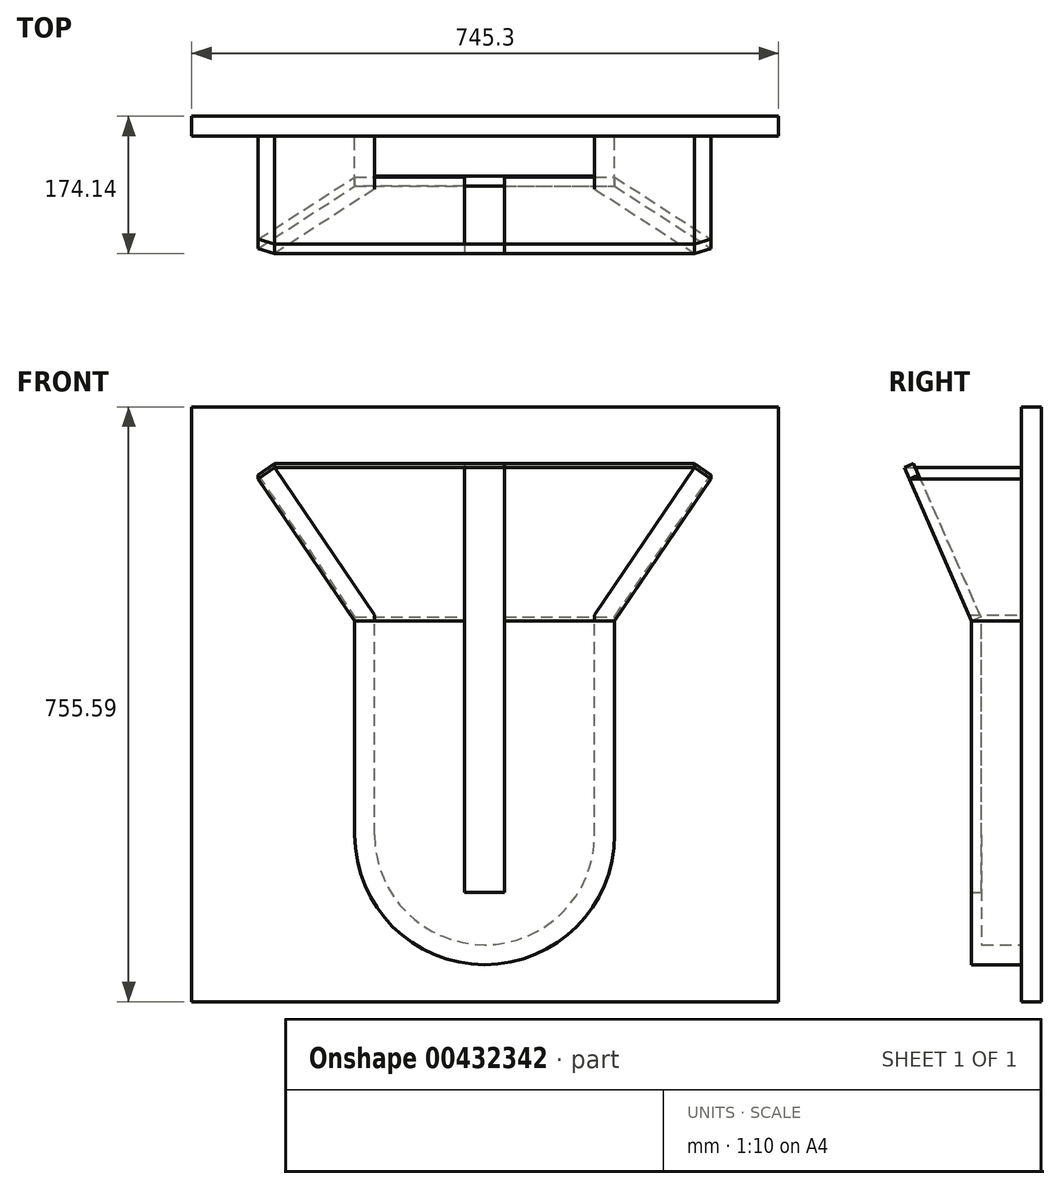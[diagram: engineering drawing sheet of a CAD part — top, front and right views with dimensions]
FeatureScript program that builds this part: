
annotation { "Feature Type Name" : "Feature", "Feature Type Description" : "" }
export const myFeature = defineFeature(function(context is Context, id is Id, definition is map)
    precondition{}
    {
        {
            var Q0;
            Q0=qCreatedBy(makeId("Front.planeOp"),FACE);
            var sketch = newSketch(context, id + "F0", { "sketchPlane" : qUnion([Q0])});
            skLineSegment(sketch, "E0.bottom", {"start": v(-216.96, 293.83) * mm, "end": v(316.44, 293.83) * mm});
            skLineSegment(sketch, "E0.top", {"start": v(-216.96, -337.7) * mm, "end": v(316.44, -337.7) * mm});
            skLineSegment(sketch, "E0.left", {"start": v(-216.96, 248.62) * mm, "end": v(-216.96, -337.7) * mm});
            skLineSegment(sketch, "E0.right", {"start": v(316.44, 248.62) * mm, "end": v(316.44, -337.7) * mm});
            skArc(sketch, "E1", {"start": v(-89.96, -172.6) * mm, "mid": v(49.74, -312.3) * mm, "end": v(189.44, -172.6) * mm});
            skLineSegment(sketch, "E2", {"start": v(-89.96, -172.6) * mm, "end": v(-89.96, 106.8) * mm});
            skLineSegment(sketch, "E3", {"start": v(189.44, -172.6) * mm, "end": v(189.44, 106.8) * mm});
            skLineSegment(sketch, "E4", {"start": v(189.44, 106.8) * mm, "end": v(316.44, 293.83) * mm});
            skLineSegment(sketch, "E5", {"start": v(-89.96, 106.8) * mm, "end": v(-216.96, 293.83) * mm});
            skLineSegment(sketch, "E6.0", {"start": v(210.46, 92.54) * mm, "end": v(337.46, 279.56) * mm});
            skLineSegment(sketch, "E7.0", {"start": v(214.84, -172.6) * mm, "end": v(214.84, 106.8) * mm});
            skArc(sketch, "E8.0", {"start": v(-115.36, -172.6) * mm, "mid": v(49.74, -337.7) * mm, "end": v(214.84, -172.6) * mm});
            skLineSegment(sketch, "E9.0", {"start": v(-115.36, -172.6) * mm, "end": v(-115.36, 106.8) * mm});
            skLineSegment(sketch, "E10.0", {"start": v(-110.97, 92.54) * mm, "end": v(-237.97, 279.56) * mm});
            skLineSegment(sketch, "E11", {"start": v(-237.97, 279.56) * mm, "end": v(-216.96, 293.83) * mm});
            skLineSegment(sketch, "E12", {"start": v(337.46, 279.56) * mm, "end": v(316.44, 293.83) * mm});
            skSolve(sketch);
        }
        {
            var Q0;
            Q0=makeQuery(id+"F0.imprint","IMPRINT",FACE,{"disambiguationData":[TD([[makeQuery(id+"F0.imprint","IMPRINT",EDGE,{"derivedFrom":sQuery(id+"F0.wireOp",EDGE,"E1")}),-1.0]])]});
            extrude(context, id + "F1", {"entities" : qUnion([Q0]), "depth" : 50.8 * mm});
        }
        {
            var Q0;
            Q0=makeQuery(id+"F1.opExtrude","CAP_FACE",FACE,{"disambiguationData":[OSD([sQuery(id+"F0.wireOp",EDGE,"E1"),sQuery(id+"F0.wireOp",EDGE,"E2"),sQuery(id+"F0.wireOp",EDGE,"E3"),sQuery(id+"F0.wireOp",EDGE,"E4"),sQuery(id+"F0.wireOp",EDGE,"E5"),sQuery(id+"F0.wireOp",EDGE,"E6.0"),sQuery(id+"F0.wireOp",EDGE,"E7.0"),sQuery(id+"F0.wireOp",EDGE,"E8.0"),sQuery(id+"F0.wireOp",EDGE,"E9.0"),sQuery(id+"F0.wireOp",EDGE,"E10.0"),sQuery(id+"F0.wireOp",EDGE,"E11"),sQuery(id+"F0.wireOp",EDGE,"E12")])],"isStart":true});
            var sketch = newSketch(context, id + "F2", { "sketchPlane" : qUnion([Q0])});
            skLineSegment(sketch, "E13.bottom", {"start": v(-423.1, 371) * mm, "end": v(322.2, 371) * mm});
            skLineSegment(sketch, "E13.top", {"start": v(-423.1, -384.6) * mm, "end": v(322.2, -384.6) * mm});
            skLineSegment(sketch, "E13.left", {"start": v(-423.1, 371) * mm, "end": v(-423.1, -384.6) * mm});
            skLineSegment(sketch, "E13.right", {"start": v(322.2, 371) * mm, "end": v(322.2, -384.6) * mm});
            skSolve(sketch);
        }
        {
            var Q0;
            Q0=makeQuery(id+"F2.imprint","IMPRINT",FACE,{"disambiguationData":[TD([[makeQuery(id+"F2.imprint","IMPRINT",EDGE,{"derivedFrom":sQuery(id+"F2.wireOp",EDGE,"E13.bottom")}),-1.0]])]});
            var Q1;
            Q1=makeQuery(id+"F2.imprint","IMPRINT",FACE,{"disambiguationData":[TD([[makeQuery(id+"F2.imprint","IMPRINT",EDGE,{"derivedFrom":makeQuery(id+"F1.opExtrude","CAP_EDGE",EDGE,{"disambiguationData":[OSD([sQuery(id+"F0.wireOp",EDGE,"E1")])],"isStart":true})}),1.0]])]});
            extrude(context, id + "F3", {"entities" : qUnion([Q0, Q1]), "operationType" : NewBodyOperationType.ADD, "depth" : 25.4 * mm});
        }
        {
            var Q0;
            Q0=makeQuery(id+"F1.opExtrude","CAP_FACE",FACE,{"disambiguationData":[OSD([sQuery(id+"F0.wireOp",EDGE,"E1"),sQuery(id+"F0.wireOp",EDGE,"E2"),sQuery(id+"F0.wireOp",EDGE,"E3"),sQuery(id+"F0.wireOp",EDGE,"E4"),sQuery(id+"F0.wireOp",EDGE,"E5"),sQuery(id+"F0.wireOp",EDGE,"E6.0"),sQuery(id+"F0.wireOp",EDGE,"E7.0"),sQuery(id+"F0.wireOp",EDGE,"E8.0"),sQuery(id+"F0.wireOp",EDGE,"E9.0"),sQuery(id+"F0.wireOp",EDGE,"E10.0"),sQuery(id+"F0.wireOp",EDGE,"E11"),sQuery(id+"F0.wireOp",EDGE,"E12")])],"isStart":false});
            var sketch = newSketch(context, id + "F4", { "sketchPlane" : qUnion([Q0])});
            skLineSegment(sketch, "E14", {"start": v(-89.96, 99) * mm, "end": v(-89.96, 106.8) * mm});
            skLineSegment(sketch, "E15", {"start": v(214.84, 99) * mm, "end": v(189.44, 99) * mm});
            skLineSegment(sketch, "E16", {"start": v(-115.36, 99) * mm, "end": v(-89.96, 99) * mm});
            skLineSegment(sketch, "E17", {"start": v(-89.96, 99) * mm, "end": v(-115.36, 99) * mm});
            skLineSegment(sketch, "E18", {"start": v(-115.36, 99) * mm, "end": v(-115.36, -172.6) * mm});
            skLineSegment(sketch, "E19", {"start": v(214.84, 99) * mm, "end": v(214.84, -172.6) * mm});
            skArc(sketch, "E20", {"start": v(-115.36, -172.6) * mm, "mid": v(49.74, -337.7) * mm, "end": v(214.84, -172.6) * mm});
            skLineSegment(sketch, "E21.trimOffspring", {"start": v(188.16, -172.6) * mm, "end": v(189.44, -172.6) * mm});
            skLineSegment(sketch, "E22", {"start": v(49.74, -172.6) * mm, "end": v(75.14, -172.6) * mm});
            skLineSegment(sketch, "E23", {"start": v(75.14, -172.6) * mm, "end": v(24.34, -172.6) * mm});
            skLineSegment(sketch, "E24.top", {"start": v(75.14, -245.78) * mm, "end": v(24.34, -245.78) * mm});
            skLineSegment(sketch, "E24.left", {"start": v(75.14, -172.6) * mm, "end": v(75.14, -245.78) * mm});
            skLineSegment(sketch, "E24.right", {"start": v(24.34, -172.6) * mm, "end": v(24.34, -245.78) * mm});
            skLineSegment(sketch, "E25.bottom", {"start": v(24.34, -172.6) * mm, "end": v(75.14, -172.6) * mm});
            skLineSegment(sketch, "E25.top", {"start": v(24.34, 99) * mm, "end": v(75.14, 99) * mm});
            skLineSegment(sketch, "E25.left", {"start": v(24.34, -172.6) * mm, "end": v(24.34, 99) * mm});
            skLineSegment(sketch, "E25.right", {"start": v(75.14, -172.6) * mm, "end": v(75.14, 99) * mm});
            skLineSegment(sketch, "E26", {"start": v(24.34, 99) * mm, "end": v(-115.36, 99) * mm});
            skLineSegment(sketch, "E27", {"start": v(75.14, 99) * mm, "end": v(214.84, 99) * mm});
            skPoint(sketch, "E28.end.orphan", {"position": v(189.44, 106.8) * mm});
            skSolve(sketch);
        }
        {
            var Q0;
            Q0=makeQuery(id+"F4.imprint","IMPRINT",FACE,{"disambiguationData":[TD([[makeQuery(id+"F4.imprint","IMPRINT",EDGE,{"derivedFrom":sQuery(id+"F4.wireOp",EDGE,"E24.top")}),1.0]])]});
            var Q1;
            {var subQ1=sQuery(id+"F4.wireOp",EDGE,"E18");Q1=makeQuery(id+"F4.imprint","IMPRINT",FACE,{"disambiguationData":[TD([[makeQuery(id+"F4.imprint","IMPRINT",EDGE,{"derivedFrom":subQ1}),-1.0]])]});}
            extrude(context, id + "F5", {"entities" : qUnion([Q0, Q1]), "operationType" : NewBodyOperationType.ADD, "depth" : 12.7 * mm});
        }
        {
            var Q0;
            {var subQ0=sQuery(id+"F0.wireOp",EDGE,"E9.0");var subQ1=sQuery(id+"F0.wireOp",EDGE,"E10.0");var subQ2=sQuery(id+"F0.wireOp",EDGE,"E5");var subQ4=sQuery(id+"F0.wireOp",EDGE,"E2");var subQ6=sQuery(id+"F0.wireOp",EDGE,"E11");Q0=makeQuery(id+"F5.boolean.opBoolean","SPLIT",FACE,{"disambiguationData":[TD([makeQuery(id+"F1.opExtrude","SWEPT_FACE",FACE,{"disambiguationData":[OSD([subQ4])]})])],"derivedFrom":makeQuery(id+"F1.opExtrude","CAP_FACE",FACE,{"disambiguationData":[OSD([sQuery(id+"F0.wireOp",EDGE,"E1"),subQ4,sQuery(id+"F0.wireOp",EDGE,"E3"),sQuery(id+"F0.wireOp",EDGE,"E4"),subQ2,sQuery(id+"F0.wireOp",EDGE,"E6.0"),sQuery(id+"F0.wireOp",EDGE,"E7.0"),sQuery(id+"F0.wireOp",EDGE,"E8.0"),subQ0,subQ1,subQ6,sQuery(id+"F0.wireOp",EDGE,"E12")])],"isStart":false})});}
            var sketch = newSketch(context, id + "F6", { "sketchPlane" : qUnion([Q0])});
            skLineSegment(sketch, "E29", {"start": v(-115.36, 99) * mm, "end": v(-89.96, 99) * mm});
            skLineSegment(sketch, "E30", {"start": v(-89.96, 99) * mm, "end": v(-89.96, 106.8) * mm});
            skLineSegment(sketch, "E31", {"start": v(-89.96, 106.8) * mm, "end": v(-216.96, 293.83) * mm});
            skLineSegment(sketch, "E32", {"start": v(-216.96, 293.83) * mm, "end": v(-237.97, 279.56) * mm});
            skLineSegment(sketch, "E33", {"start": v(-237.97, 279.56) * mm, "end": v(-118.5, 103.63) * mm});
            skSolve(sketch);
        }
        {
            var Q0;
            {var subQ0=sQuery(id+"F6.wireOp",EDGE,"E29");Q0=makeQuery(id+"F6.imprint","IMPRINT",FACE,{"disambiguationData":[TD([[makeQuery(id+"F6.imprint","IMPRINT",EDGE,{"derivedFrom":subQ0}),-1.0]])]});}
            extrude(context, id + "F7", {"entities" : qUnion([Q0]), "operationType" : NewBodyOperationType.ADD, "depth" : 101.6 * mm});
        }
        {
            var Q0;
            Q0=makeQuery(id+"F7.opExtrude","CAP_EDGE",EDGE,{"disambiguationData":[OSD([sQuery(id+"F6.wireOp",EDGE,"E29")])],"isStart":false});
            chamfer(context, id + "F8", {"entities" : qUnion([Q0]), "chamferType" : ChamferType.TWO_OFFSETS, "width1" : 88.9 * mm, "oppositeDirection" : false, "width2" : 203.2 * mm});
        }
        {
            var Q0;
            {var subQ0=sQuery(id+"F0.wireOp",EDGE,"E7.0");var subQ1=sQuery(id+"F0.wireOp",EDGE,"E6.0");var subQ4=sQuery(id+"F0.wireOp",EDGE,"E4");var subQ5=sQuery(id+"F0.wireOp",EDGE,"E3");var subQ6=sQuery(id+"F0.wireOp",EDGE,"E12");Q0=makeQuery(id+"F5.boolean.opBoolean","SPLIT",FACE,{"disambiguationData":[TD([makeQuery(id+"F1.opExtrude","SWEPT_FACE",FACE,{"disambiguationData":[OSD([subQ5])]})])],"derivedFrom":makeQuery(id+"F1.opExtrude","CAP_FACE",FACE,{"disambiguationData":[OSD([sQuery(id+"F0.wireOp",EDGE,"E1"),sQuery(id+"F0.wireOp",EDGE,"E2"),subQ5,subQ4,sQuery(id+"F0.wireOp",EDGE,"E5"),subQ1,subQ0,sQuery(id+"F0.wireOp",EDGE,"E8.0"),sQuery(id+"F0.wireOp",EDGE,"E9.0"),sQuery(id+"F0.wireOp",EDGE,"E10.0"),sQuery(id+"F0.wireOp",EDGE,"E11"),subQ6])],"isStart":false})});}
            extrude(context, id + "F9", {"entities" : qUnion([Q0]), "operationType" : NewBodyOperationType.ADD, "depth" : 101.6 * mm});
        }
        {
            var Q0;
            Q0=makeQuery(id+"F9.opExtrude","CAP_EDGE",EDGE,{"disambiguationData":[OSD([sQuery(id+"F4.wireOp",EDGE,"E27")])],"isStart":false});
            chamfer(context, id + "F10", {"entities" : qUnion([Q0]), "chamferType" : ChamferType.TWO_OFFSETS, "width1" : 203.2 * mm, "oppositeDirection" : false, "width2" : 88.9 * mm, "tangentPropagation" : true});
        }
        {
            var Q0;
            Q0=makeQuery(id+"F8.opChamfer","BLEND_FACE",FACE,{"disambiguationData":[OSD([sQuery(id+"F6.wireOp",EDGE,"E29")])]});
            var sketch = newSketch(context, id + "F11", { "sketchPlane" : qUnion([Q0])});
            skLineSegment(sketch, "E34", {"start": v(-115.36, 116.15) * mm, "end": v(214.84, 116.15) * mm});
            skLineSegment(sketch, "E35", {"start": v(-115.36, 116.15) * mm, "end": v(-237.97, 313.24) * mm});
            skLineSegment(sketch, "E36", {"start": v(-237.97, 313.24) * mm, "end": v(-216.96, 328.81) * mm});
            skLineSegment(sketch, "E37", {"start": v(214.84, 116.15) * mm, "end": v(337.46, 313.24) * mm});
            skLineSegment(sketch, "E38", {"start": v(337.46, 313.24) * mm, "end": v(316.45, 328.8) * mm});
            skLineSegment(sketch, "E39", {"start": v(-216.96, 328.81) * mm, "end": v(316.45, 328.8) * mm});
            skLineSegment(sketch, "E40.bottom", {"start": v(24.34, 116.15) * mm, "end": v(75.14, 116.15) * mm});
            skLineSegment(sketch, "E40.top", {"start": v(24.34, 328.81) * mm, "end": v(75.14, 328.81) * mm});
            skLineSegment(sketch, "E40.left", {"start": v(24.34, 116.15) * mm, "end": v(24.34, 328.81) * mm});
            skLineSegment(sketch, "E40.right", {"start": v(75.14, 116.15) * mm, "end": v(75.14, 328.81) * mm});
            skSolve(sketch);
        }
        {
            var Q0;
            {var subQ6=sQuery(id+"F11.wireOp",EDGE,"E40.top");Q0=makeQuery(id+"F11.imprint","IMPRINT",FACE,{"disambiguationData":[TD([[makeQuery(id+"F11.imprint","IMPRINT",EDGE,{"derivedFrom":subQ6}),1.0]])]});}
            var Q1;
            {var subQ3=sQuery(id+"F11.wireOp",EDGE,"E37");Q1=makeQuery(id+"F11.imprint","IMPRINT",FACE,{"disambiguationData":[TD([[makeQuery(id+"F11.imprint","IMPRINT",EDGE,{"derivedFrom":subQ3}),1.0]])]});}
            var Q2;
            {var subQ2=sQuery(id+"F11.wireOp",EDGE,"E35");Q2=makeQuery(id+"F11.imprint","IMPRINT",FACE,{"disambiguationData":[TD([[makeQuery(id+"F11.imprint","IMPRINT",EDGE,{"derivedFrom":subQ2}),-1.0]])]});}
            extrude(context, id + "F12", {"entities" : qUnion([Q0, Q1, Q2]), "oppositeDirection" : true, "depth" : 12.7 * mm});
        }
    });
